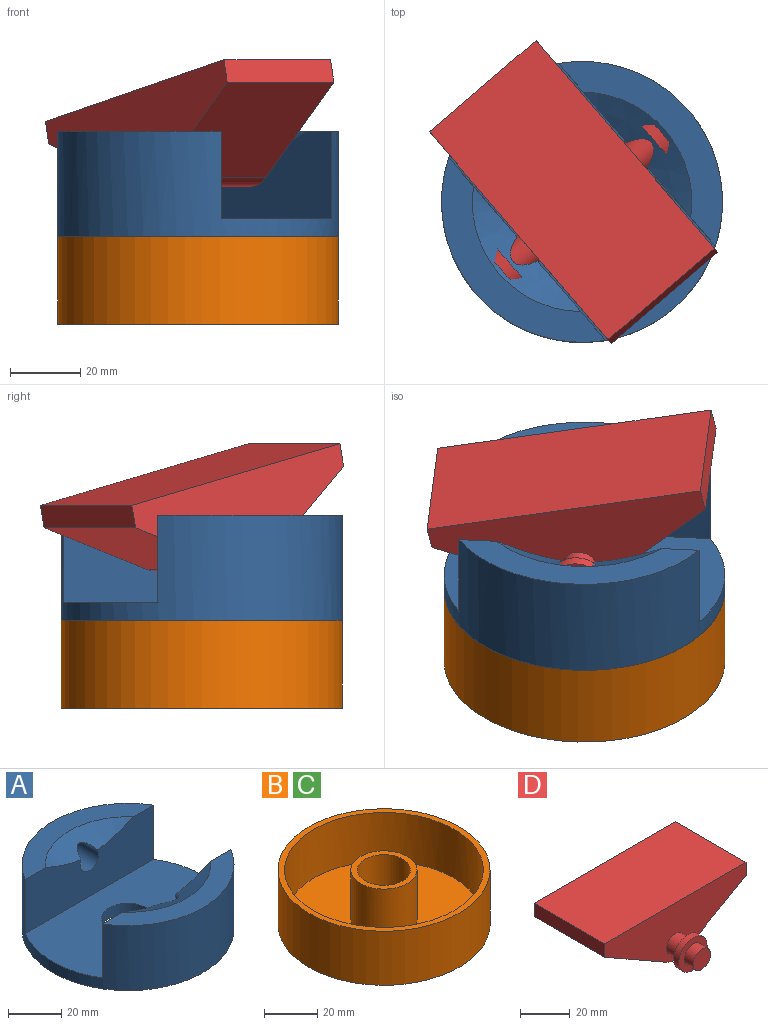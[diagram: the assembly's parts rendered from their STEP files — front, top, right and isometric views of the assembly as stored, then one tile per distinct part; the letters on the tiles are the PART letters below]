
ASSEMBLY  parts=4 mates=2
PART A: 30 faces, bbox 80x80x30 mm
  f0: plane 25x25mm, normal (0,0,-1), area 176.7mm2, adj f5,f24
  f1: cone r=31.24mm half-angle=60.3deg, axis (0,0,1), area 359.3mm2, adj f3,f8,f13
  f2: cone r=31.24mm half-angle=60.3deg, axis (0,0,1), area 359.3mm2, adj f6,f9,f12
  f3: plane 68.58x19.4mm, normal (0,0,1), area 594.7mm2, adj f1,f4,f8
  f4: cylinder r=40mm len=80mm, axis (0,0,1), area 5375.8mm2, adj f3,f6,f7,f8,f9,f10
  f5: cylinder r=10mm len=20mm, axis (0,0,1), area 314.2mm2, adj f0,f10
  f6: plane 68.58x19.4mm, normal (0,0,1), area 594.7mm2, adj f2,f4,f9
  f7: plane 80x80mm, normal (0,0,-1), area 608.7mm2, adj f4,f23
  f8: plane 68.58x25.01mm, normal (0,-1,0), area 1473.2mm2, adj f1,f3,f4,f10,f13
  f9: plane 68.58x25.01mm, normal (0,1,0), area 1473.2mm2, adj f2,f4,f6,f10,f12
  f10: plane 80x41.2mm, normal (0,0,1), area 2829.7mm2, adj f4,f5,f8,f9
  f11: plane 10x10mm, normal (0,1,0), area 78.5mm2, adj f12
  f12: cylinder r=5mm len=14.4mm, axis (0,1,0), area 413.3mm2, adj f2,f9,f11
  f13: cylinder r=5mm len=14.4mm, axis (0,1,0), area 413.3mm2, adj f1,f8,f14
  f14: plane 10x10mm, normal (0,-1,0), area 78.5mm2, adj f13
  f15: cylinder r=7.5mm len=15mm, axis (0,1,0), area 458.4mm2, adj f17,f18,f21,f23,f25,f27
  f16: plane 24.44x14.05mm, normal (0,0,-1), area 134.8mm2, adj f20,f23,f26,f29
  f17: plane 24.44x14.05mm, normal (0,0,-1), area 134.8mm2, adj f15,f21,f23,f27
  f18: cone r=32.48mm half-angle=60.3deg, axis (0,0,1), area 89.4mm2, adj f15,f25,f27
  f19: cone r=32.48mm half-angle=60.3deg, axis (0,0,1), area 89.4mm2, adj f22,f26,f29
  f20: cone r=32.48mm half-angle=60.3deg, axis (0,0,1), area 89.4mm2, adj f16,f26,f29
  f21: cone r=32.48mm half-angle=60.3deg, axis (0,0,1), area 89.4mm2, adj f15,f17,f27
  f22: plane 24.44x14.05mm, normal (0,0,-1), area 134.8mm2, adj f19,f23,f26,f29
  f23: cylinder r=37.5mm len=75mm, axis (0,0,1), area 3663.7mm2, adj f7,f15,f16,f17,f22,f25,f26,f27
  f24: cylinder r=12.5mm len=25mm, axis (0,0,1), area 196.3mm2, adj f0,f28
  f25: plane 24.44x14.05mm, normal (0,0,-1), area 134.8mm2, adj f15,f18,f23,f27
  f26: plane 59.08x25mm, normal (0,1,0), area 1235.5mm2, adj f16,f19,f20,f22,f23,f28,f29
  f27: plane 59.08x25mm, normal (0,-1,0), area 1235.5mm2, adj f15,f17,f18,f21,f23,f25,f28
  f28: plane 75x46.2mm, normal (0,0,-1), area 2740.4mm2, adj f23,f24,f26,f27
  f29: cylinder r=7.5mm len=15mm, axis (0,1,0), area 458.4mm2, adj f16,f19,f20,f22,f23,f26
PART B: 8 faces, bbox 80x80x25 mm
  f0: plane 25x25mm, normal (0,0,1), area 176.7mm2, adj f1,f5
  f1: cylinder r=10mm len=25mm, axis (0,0,-1), area 1570.8mm2, adj f0,f4
  f2: plane 80x80mm, normal (0,0,1), area 608.7mm2, adj f3,f6
  f3: cylinder r=40mm len=80mm, axis (0,0,-1), area 6283.2mm2, adj f2,f4
  f4: plane 80x80mm, normal (0,0,-1), area 4712.4mm2, adj f1,f3
  f5: cylinder r=12.5mm len=25mm, axis (0,0,-1), area 1767.1mm2, adj f0,f7
  f6: cylinder r=37.5mm len=75mm, axis (0,0,-1), area 5301.4mm2, adj f2,f7
  f7: plane 75x75mm, normal (0,0,1), area 3927mm2, adj f5,f6
PART C: same geometry as B
PART D: 20 faces, bbox 80x70x28 mm
  f0: cylinder r=8mm len=16mm, axis (0,1,0), area 150.8mm2, adj f1,f2
  f1: plane 16x16mm, normal (0,-1,0), area 122.5mm2, adj f0,f19
  f2: plane 16x16mm, normal (0,1,0), area 122.5mm2, adj f0,f17
  f3: cylinder r=5mm len=10mm, axis (0,1,0), area 157.1mm2, adj f4,f15
  f4: plane 10x10mm, normal (0,1,0), area 78.5mm2, adj f3
  f5: cylinder r=5mm len=10mm, axis (0,1,0), area 219.9mm2, adj f13,f14
  f6: plane 80x40mm, normal (0,0,1), area 3200mm2, adj f7,f11,f12,f13
  f7: plane 40x6.5mm, normal (-1,0,0), area 260mm2, adj f6,f8,f12,f13
  f8: plane 40x35.04mm, normal (-0.5,0,-0.87), area 1614mm2, adj f7,f9,f12,f13
  f9: cylinder r=10mm len=40mm, axis (0,1,0), area 415mm2, adj f8,f10,f12,f13
  f10: plane 40x35.04mm, normal (0.5,0,-0.87), area 1614mm2, adj f9,f11,f12,f13
  f11: plane 40x6.5mm, normal (1,0,0), area 260mm2, adj f6,f10,f12,f13
  f12: plane 80x27.82mm, normal (0,-1,0), area 1349.8mm2, adj f6,f7,f8,f9,f10,f11,f17
  f13: plane 80x27.82mm, normal (0,1,0), area 1349.8mm2, adj f5,f6,f7,f8,f9,f10,f11
  f14: plane 16x16mm, normal (0,-1,0), area 122.5mm2, adj f5,f16
  f15: plane 16x16mm, normal (0,1,0), area 122.5mm2, adj f3,f16
  f16: cylinder r=8mm len=16mm, axis (0,-1,0), area 150.8mm2, adj f14,f15
  f17: cylinder r=5mm len=10mm, axis (0,1,0), area 219.9mm2, adj f2,f12
  f18: plane 10x10mm, normal (0,-1,0), area 78.5mm2, adj f19
  f19: cylinder r=5mm len=10mm, axis (0,1,0), area 157.1mm2, adj f1,f18
PLACE A rot(axis=(0,0,-1),49.4deg) t=(0,0,27.5)mm
PLACE B at identity
PLACE C at identity fixed
PLACE D rot(axis=(-0.11,0.05,0.99),130.9deg) t=(0,0,34.5)mm
MATE revolute D.f3 <-> A.f12  axis (0.76,0.65,0) through (26.56,22.79,34.5)mm
MATE revolute C.f1 <-> A.f1  axis (0,0,1) through (0,0,12.5)mm
